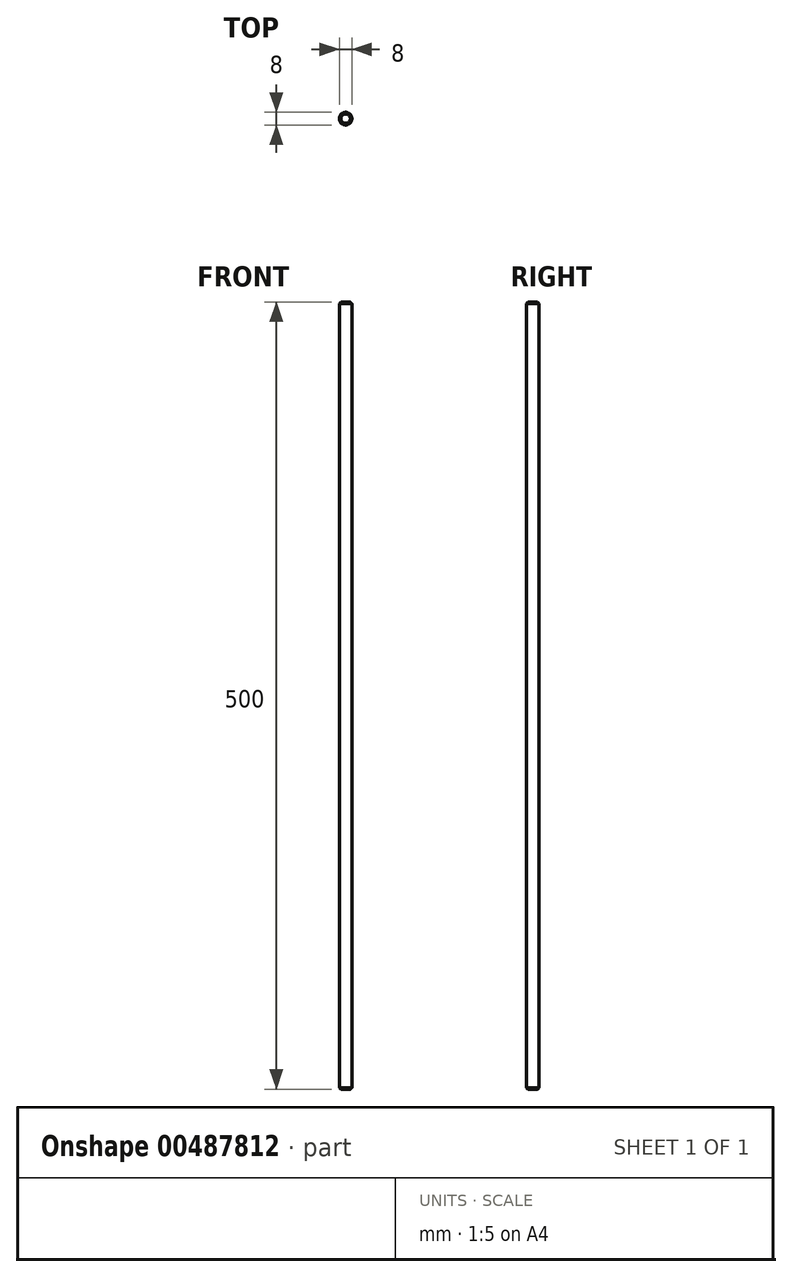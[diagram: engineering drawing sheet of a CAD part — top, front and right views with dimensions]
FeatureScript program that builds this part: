
annotation { "Feature Type Name" : "Feature", "Feature Type Description" : "" }
export const myFeature = defineFeature(function(context is Context, id is Id, definition is map)
    precondition{}
    {
        {
            var Q0;
            Q0=qCreatedBy(makeId("Top.planeOp"),FACE);
            var sketch = newSketch(context, id + "F0", { "sketchPlane" : qUnion([Q0])});
            skCircle(sketch, "E0", {"center": v(0, 0) * mm, "radius": 4 * mm});
            skSolve(sketch);
        }
        {
            var Q0;
            Q0 = qSketchRegion(id + "F0", true);
            extrude(context, id + "F1", {"entities" : qUnion([Q0]), "endBound" : BoundingType.SYMMETRIC, "oppositeDirection" : true, "depth" : 500 * mm, "offsetDistance" : 25 * mm});
        }
        {
            var Q0;
            Q0=makeQuery(id+"F1.opExtrude","CAP_EDGE",EDGE,{"disambiguationData":[OSD([sQuery(id+"F0.wireOp",EDGE,"E0")])],"isStart":true});
            var Q1;
            Q1=makeQuery(id+"F1.opExtrude","CAP_EDGE",EDGE,{"disambiguationData":[OSD([sQuery(id+"F0.wireOp",EDGE,"E0")])],"isStart":false});
            chamfer(context, id + "F2", {"entities" : qUnion([Q0, Q1]), "width" : 1 * mm, "tangentPropagation" : true});
        }
    });
